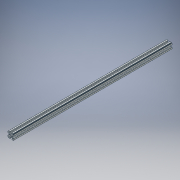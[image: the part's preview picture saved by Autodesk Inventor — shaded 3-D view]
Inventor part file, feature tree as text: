
AUTODESK INVENTOR PART (.ipt)
format: ipt  version: 2016 (Build 200138000, 138)  size: 357,888 bytes
history: native  units: in
note: dims shown in document units (in); Inventor stores cm internally (conversion verified against a paired STEP export)
features: extrude x1, sketch x1, fillet x1
ambient origin geometry x8: Origin, YZ Plane, XZ Plane, XY Plane, X Axis, Y Axis, Z Axis, Center Point
bodies: Solid1 (feature_tree)
feature tree (3):
  extrude  "Extrusion1"  [1 undecoded]
  sketch  "Sketch1"  dims[d0=46.0in d1=0.0in]
  fillet  "Fillet10"  [1 undecoded]
note: 2 required parameter values undecoded (feature->parameter linkage not recoverable at this tier; creation-order binding heuristic only, values carry confidence <= 0.55)
